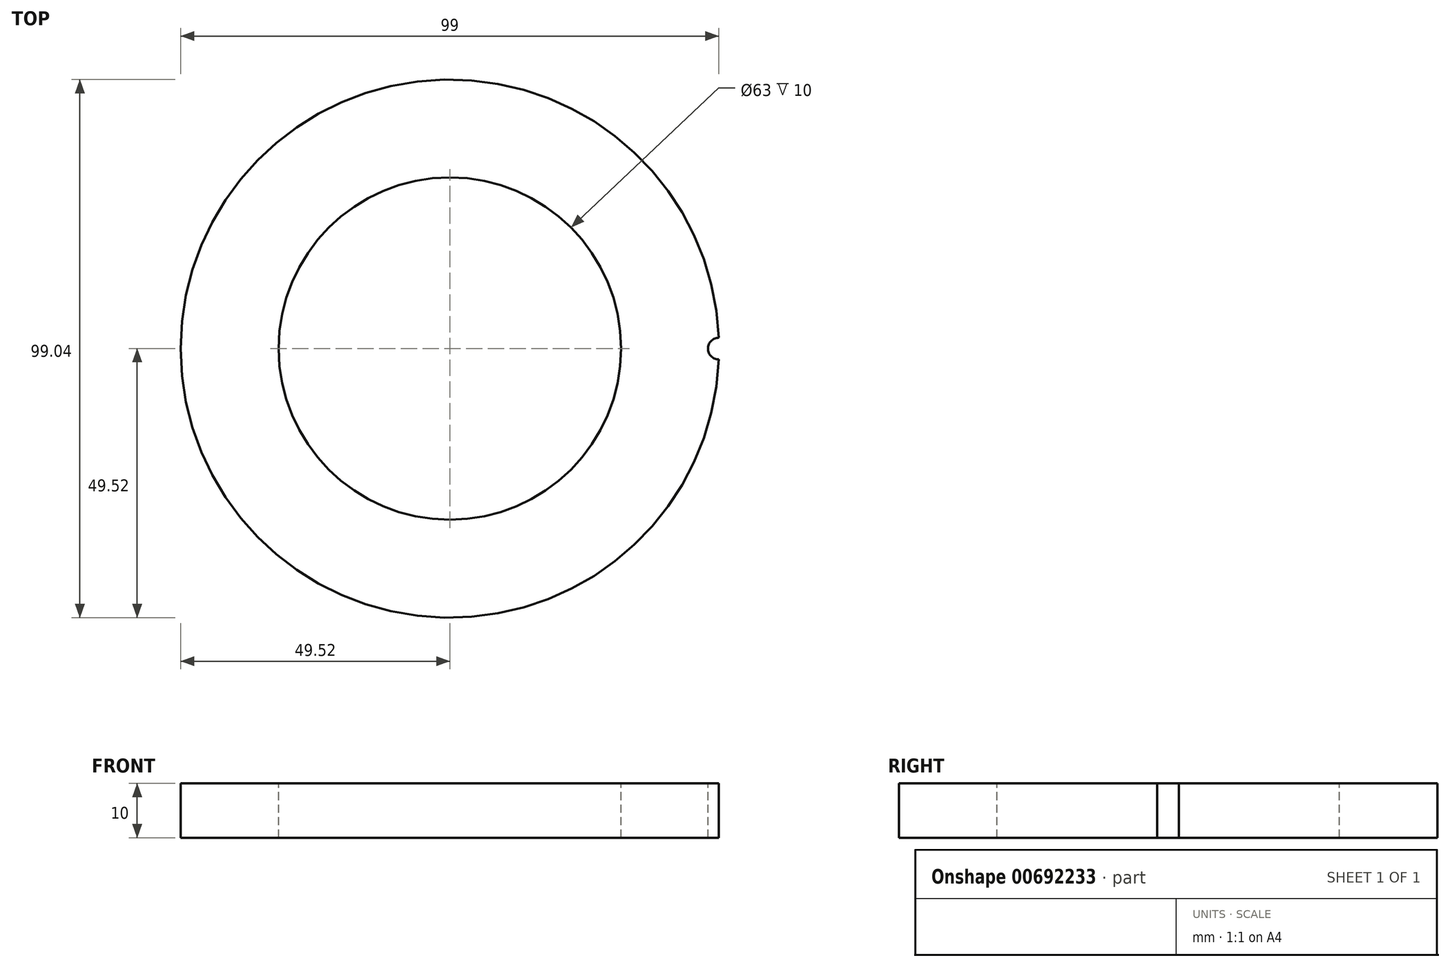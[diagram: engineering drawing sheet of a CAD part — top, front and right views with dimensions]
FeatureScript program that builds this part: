
annotation { "Feature Type Name" : "Feature", "Feature Type Description" : "" }
export const myFeature = defineFeature(function(context is Context, id is Id, definition is map)
    precondition{}
    {
        {
            var Q0;
            Q0=qCreatedBy(makeId("Front.planeOp"),FACE);
            var sketch = newSketch(context, id + "F0", { "sketchPlane" : qUnion([Q0])});
            skLineSegment(sketch, "E0", {"start": v(-49.52, 0) * mm, "end": v(-49.52, 10) * mm});
            skLineSegment(sketch, "E1", {"start": v(-49.52, 10) * mm, "end": v(-31.5, 10) * mm});
            skLineSegment(sketch, "E2", {"start": v(-31.5, 10) * mm, "end": v(-31.5, 0) * mm});
            skLineSegment(sketch, "E3", {"start": v(-31.5, 0) * mm, "end": v(-49.52, 0) * mm});
            skLineSegment(sketch, "E4", {"start": v(0, 0) * mm, "end": v(0, -9.24) * mm});
            skSolve(sketch);
        }
        {
            var Q0;
            Q0=makeQuery(id+"F0.imprint","IMPRINT",FACE,{"disambiguationData":[TD([[makeQuery(id+"F0.imprint","IMPRINT",EDGE,{"derivedFrom":sQuery(id+"F0.wireOp",EDGE,"E0")}),-1.0]])]});
            var Q1;
            Q1=sQuery(id+"F0.wireOp",EDGE,"E4");
            revolve(context, id + "F1", {"surfaceOperationType" : NewSurfaceOperationType.NEW, "entities" : qUnion([Q0]), "axis" : qUnion([Q1]), "revolveType" : RevolveType.FULL});
        }
        {
            var Q0;
            Q0=makeQuery(id+"F1.opRevolve","SWEPT_FACE",FACE,{"disambiguationData":[OSD([sQuery(id+"F0.wireOp",EDGE,"E1")])]});
            var sketch = newSketch(context, id + "F2", { "sketchPlane" : qUnion([Q0])});
            skPoint(sketch, "E5", {"position": v(49.48, 2) * mm});
            skPoint(sketch, "E6", {"position": v(49.48, -2) * mm});
            skArc(sketch, "E7", {"start": v(49.48, 2) * mm, "mid": v(47.48, 0) * mm, "end": v(49.48, -2) * mm});
            skSolve(sketch);
        }
        {
            var Q0;
            {var subQ0=sQuery(id+"F2.wireOp",EDGE,"E7");Q0=makeQuery(id+"F2.imprint","IMPRINT",FACE,{"disambiguationData":[TD([[makeQuery(id+"F2.imprint","IMPRINT",EDGE,{"derivedFrom":subQ0}),1.0]])]});}
            extrude(context, id + "F3", {"entities" : qUnion([Q0]), "operationType" : NewBodyOperationType.REMOVE, "endBound" : BoundingType.THROUGH_ALL, "oppositeDirection" : true, "depth" : 25 * mm, "offsetDistance" : 25 * mm});
        }
    });
